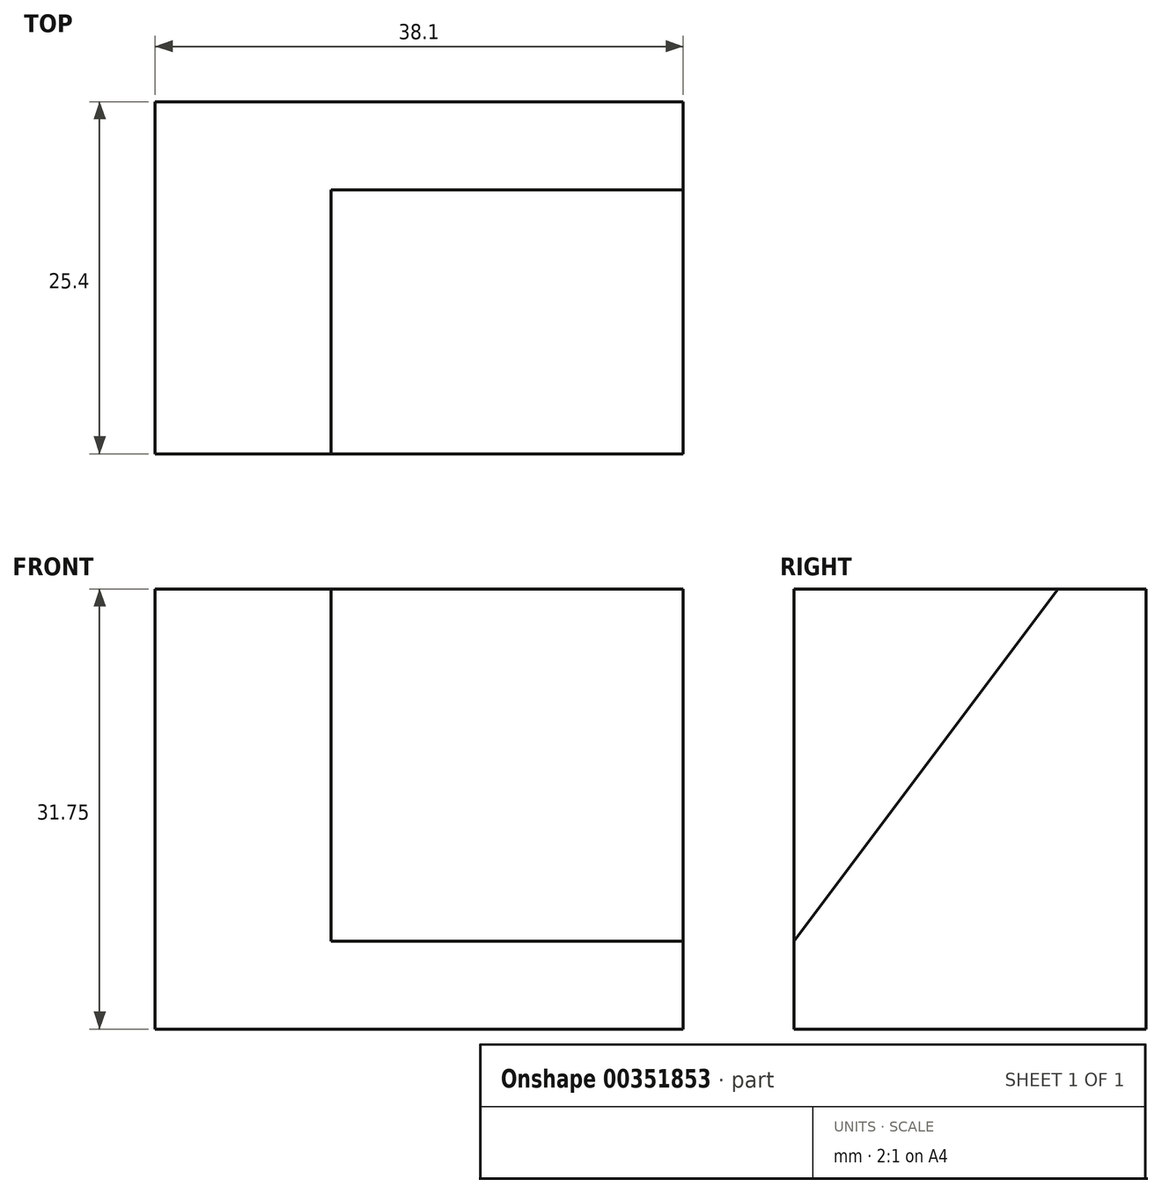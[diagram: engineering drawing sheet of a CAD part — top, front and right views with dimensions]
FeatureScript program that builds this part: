
annotation { "Feature Type Name" : "Feature", "Feature Type Description" : "" }
export const myFeature = defineFeature(function(context is Context, id is Id, definition is map)
    precondition{}
    {
        {
            var Q0;
            Q0=qCreatedBy(makeId("Right.planeOp"),FACE);
            var sketch = newSketch(context, id + "F0", { "sketchPlane" : qUnion([Q0])});
            skLineSegment(sketch, "E0.bottom", {"start": v(0, 0) * mm, "end": v(25.4, 0) * mm});
            skLineSegment(sketch, "E0.top", {"start": v(0, 31.75) * mm, "end": v(25.4, 31.75) * mm});
            skLineSegment(sketch, "E0.left", {"start": v(0, 0) * mm, "end": v(0, 31.75) * mm});
            skLineSegment(sketch, "E0.right", {"start": v(25.4, 0) * mm, "end": v(25.4, 31.75) * mm});
            skSolve(sketch);
        }
        {
            var Q0;
            Q0 = qSketchRegion(id + "F0", true);
            extrude(context, id + "F1", {"entities" : qUnion([Q0]), "depth" : 38.1 * mm});
        }
        {
            var Q0;
            Q0=makeQuery(id+"F1.opExtrude","CAP_FACE",FACE,{"disambiguationData":[OSD([sQuery(id+"F0.wireOp",EDGE,"E0.bottom"),sQuery(id+"F0.wireOp",EDGE,"E0.top"),sQuery(id+"F0.wireOp",EDGE,"E0.left"),sQuery(id+"F0.wireOp",EDGE,"E0.right")])],"isStart":false});
            var sketch = newSketch(context, id + "F2", { "sketchPlane" : qUnion([Q0])});
            skLineSegment(sketch, "E1", {"start": v(19.05, 31.75) * mm, "end": v(0, 6.35) * mm});
            skLineSegment(sketch, "E2", {"start": v(0, 6.35) * mm, "end": v(0, 31.75) * mm});
            skLineSegment(sketch, "E3", {"start": v(0, 31.75) * mm, "end": v(19.05, 31.75) * mm});
            skSolve(sketch);
        }
        {
            var Q0;
            Q0 = qSketchRegion(id + "F2", true);
            extrude(context, id + "F3", {"entities" : qUnion([Q0]), "operationType" : NewBodyOperationType.REMOVE, "oppositeDirection" : true, "depth" : 25.4 * mm});
        }
    });
